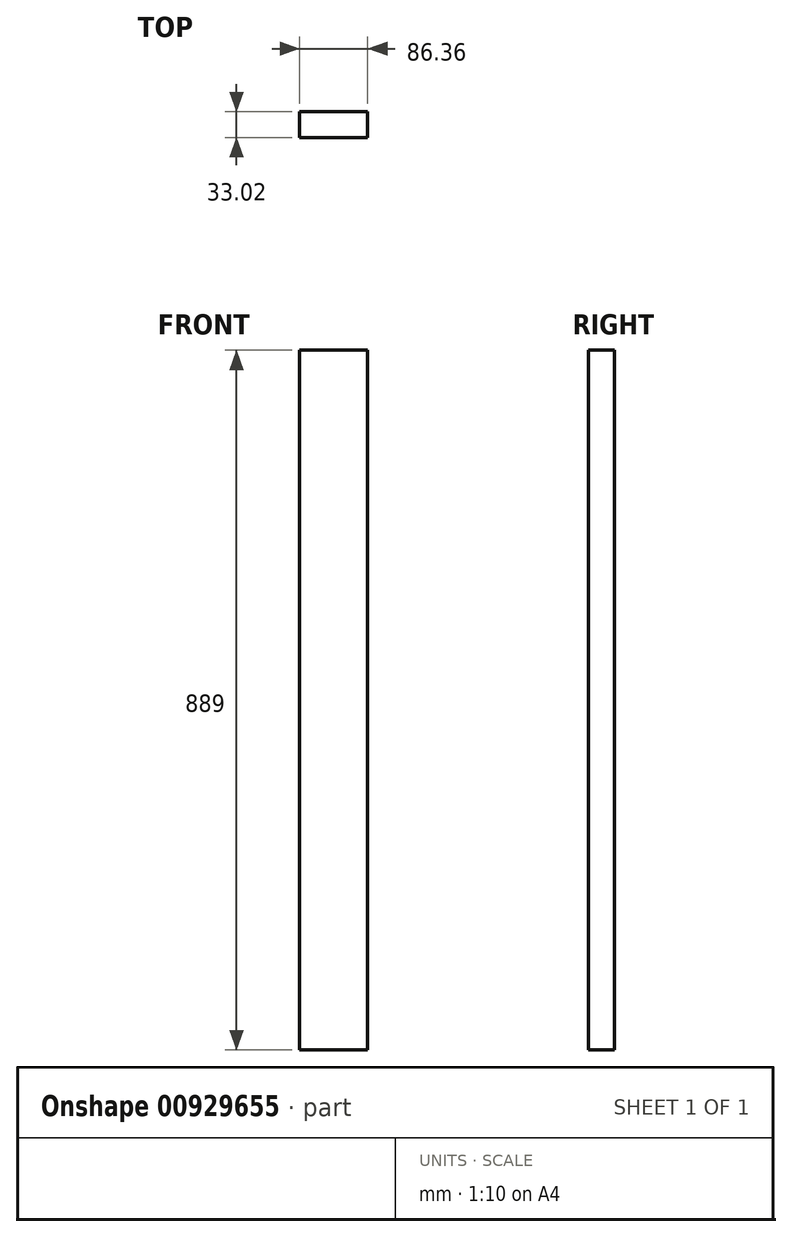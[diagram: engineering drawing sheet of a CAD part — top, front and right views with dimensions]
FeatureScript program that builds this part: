
annotation { "Feature Type Name" : "Feature", "Feature Type Description" : "" }
export const myFeature = defineFeature(function(context is Context, id is Id, definition is map)
    precondition{}
    {
        {
            var Q0;
            Q0=qCreatedBy(makeId("Front.planeOp"),FACE);
            var sketch = newSketch(context, id + "F0", { "sketchPlane" : qUnion([Q0])});
            skLineSegment(sketch, "E0.bottom", {"start": v(-43.18, -444.5) * mm, "end": v(43.18, -444.5) * mm});
            skLineSegment(sketch, "E0.top", {"start": v(-43.18, 444.5) * mm, "end": v(43.18, 444.5) * mm});
            skLineSegment(sketch, "E0.left", {"start": v(-43.18, -444.5) * mm, "end": v(-43.18, 444.5) * mm});
            skLineSegment(sketch, "E0.right", {"start": v(43.18, -444.5) * mm, "end": v(43.18, 444.5) * mm});
            skPoint(sketch, "E0.middle", {"position": v(0, 0) * mm});
            skSolve(sketch);
        }
        {
            var Q0;
            Q0 = qSketchRegion(id + "F0", true);
            extrude(context, id + "F1", {"entities" : qUnion([Q0]), "depth" : 33.02 * mm, "offsetDistance" : 25.4 * mm});
        }
    });
